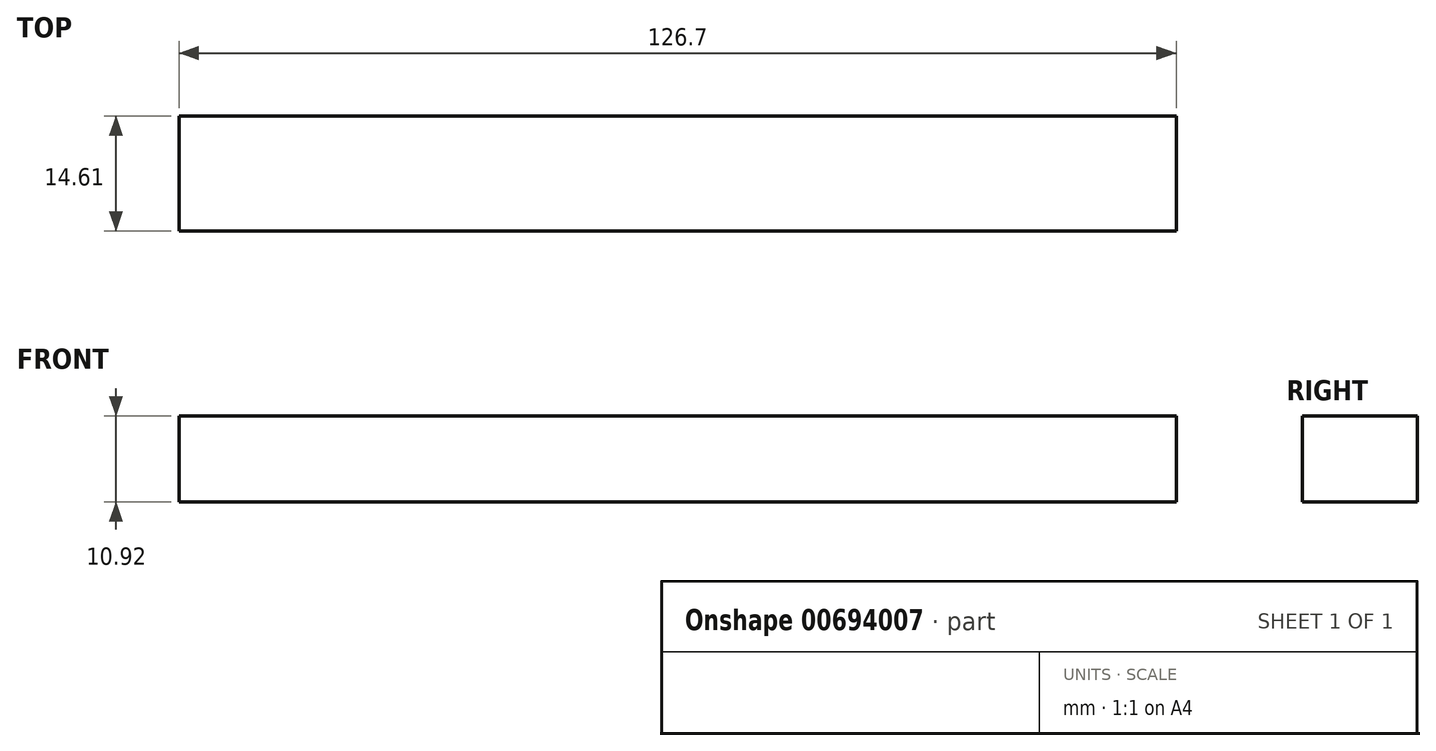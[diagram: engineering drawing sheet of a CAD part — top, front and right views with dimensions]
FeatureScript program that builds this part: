
annotation { "Feature Type Name" : "Feature", "Feature Type Description" : "" }
export const myFeature = defineFeature(function(context is Context, id is Id, definition is map)
    precondition{}
    {
        {
            var Q0;
            Q0=qCreatedBy(makeId("Top.planeOp"),FACE);
            var sketch = newSketch(context, id + "F0", { "sketchPlane" : qUnion([Q0])});
            skLineSegment(sketch, "E0.bottom", {"start": v(-60.6, 6.4) * mm, "end": v(66.09, 6.4) * mm});
            skLineSegment(sketch, "E0.top", {"start": v(-60.6, -8.22) * mm, "end": v(66.09, -8.22) * mm});
            skLineSegment(sketch, "E0.left", {"start": v(-60.6, 6.4) * mm, "end": v(-60.6, -8.22) * mm});
            skLineSegment(sketch, "E0.right", {"start": v(66.09, 6.4) * mm, "end": v(66.09, -8.22) * mm});
            skSolve(sketch);
        }
        {
            var Q0;
            Q0=makeQuery(id+"F0.imprint","IMPRINT",FACE,{"disambiguationData":[TD([[makeQuery(id+"F0.imprint","IMPRINT",EDGE,{"derivedFrom":sQuery(id+"F0.wireOp",EDGE,"E0.bottom")}),-1.0]])]});
            extrude(context, id + "F1", {"entities" : qUnion([Q0]), "oppositeDirection" : true, "depth" : 10.92 * mm, "offsetDistance" : 25.4 * mm});
        }
    });
